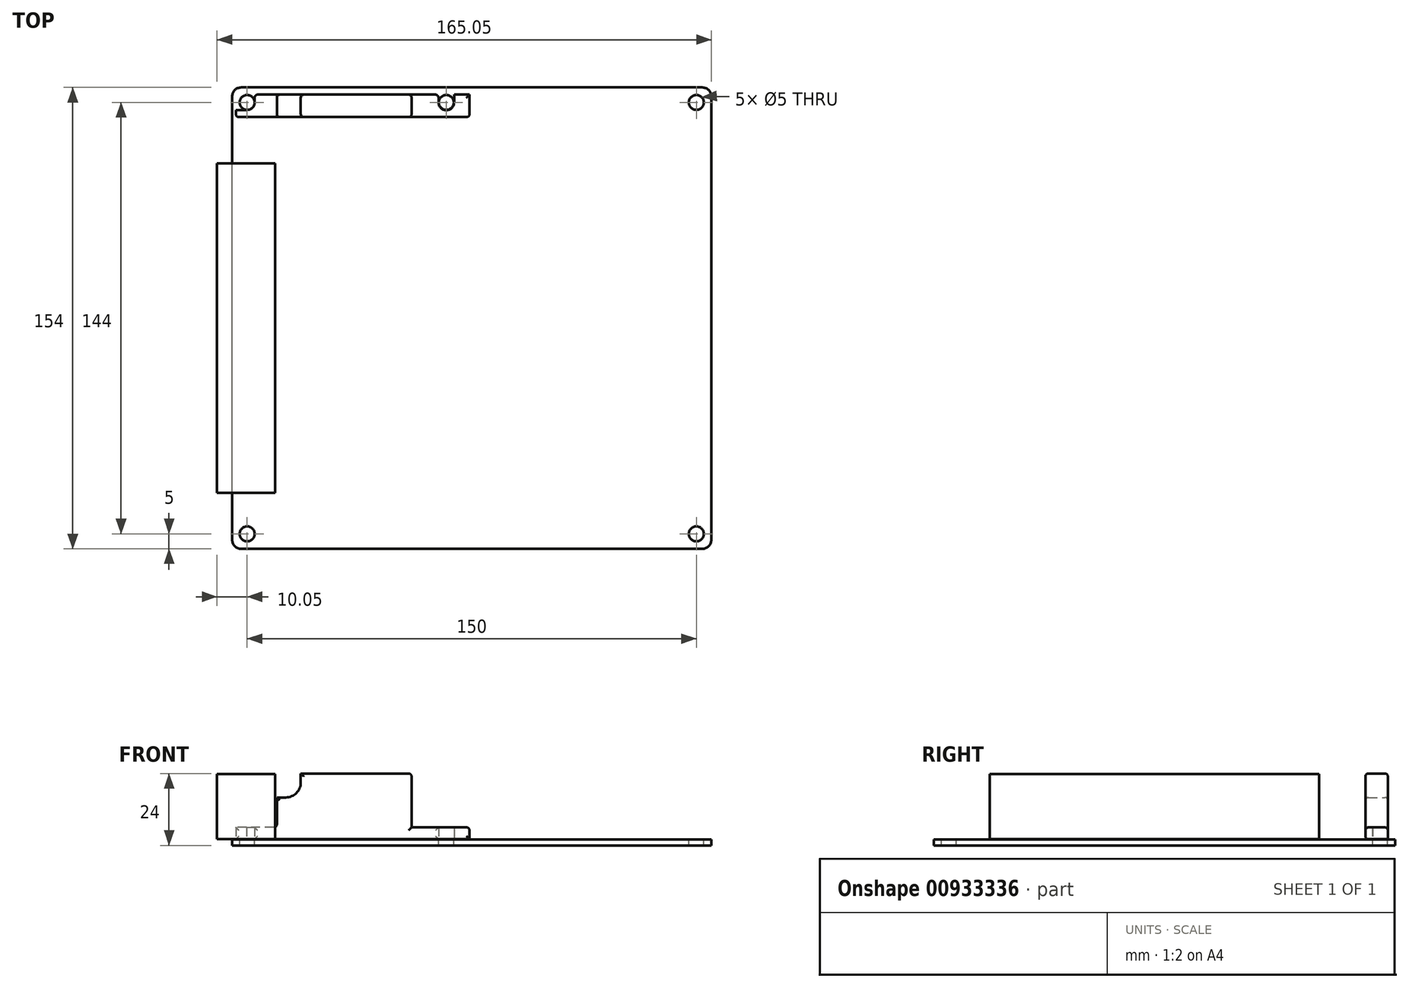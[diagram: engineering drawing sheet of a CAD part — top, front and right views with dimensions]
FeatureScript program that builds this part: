
annotation { "Feature Type Name" : "Feature", "Feature Type Description" : "" }
export const myFeature = defineFeature(function(context is Context, id is Id, definition is map)
    precondition{}
    {
        {
            var Q0;
            Q0=qCreatedBy(makeId("Top.planeOp"),FACE);
            var sketch = newSketch(context, id + "F0", { "sketchPlane" : qUnion([Q0])});
            skLineSegment(sketch, "E0.bottom", {"start": v(77, -77) * mm, "end": v(-77, -77) * mm});
            skLineSegment(sketch, "E0.top", {"start": v(77, 77) * mm, "end": v(-77, 77) * mm});
            skLineSegment(sketch, "E0.left", {"start": v(80, -74) * mm, "end": v(80, 74) * mm});
            skLineSegment(sketch, "E0.right", {"start": v(-80, -74) * mm, "end": v(-80, 74) * mm});
            skPoint(sketch, "E0.middle", {"position": v(0, 0) * mm});
            skPoint(sketch, "E1.visualSharp", {"position": v(80, 77) * mm});
            skArc(sketch, "E1.filletArc", {"start": v(80, 74) * mm, "mid": v(79.12, 76.12) * mm, "end": v(77, 77) * mm});
            skPoint(sketch, "E2.visualSharp", {"position": v(80, -77) * mm});
            skArc(sketch, "E2.filletArc", {"start": v(77, -77) * mm, "mid": v(79.12, -76.12) * mm, "end": v(80, -74) * mm});
            skPoint(sketch, "E3.visualSharp", {"position": v(-80, -77) * mm});
            skArc(sketch, "E3.filletArc", {"start": v(-80, -74) * mm, "mid": v(-79.12, -76.12) * mm, "end": v(-77, -77) * mm});
            skPoint(sketch, "E4.visualSharp", {"position": v(-80, 77) * mm});
            skArc(sketch, "E4.filletArc", {"start": v(-77, 77) * mm, "mid": v(-79.12, 76.12) * mm, "end": v(-80, 74) * mm});
            skSolve(sketch);
        }
        {
            var Q0;
            Q0 = qSketchRegion(id + "F0", true);
            extrude(context, id + "F1", {"entities" : qUnion([Q0]), "depth" : 2 * mm, "offsetDistance" : 25 * mm});
        }
        {
            var Q0;
            Q0=makeQuery(id+"F1.opExtrude","CAP_FACE",FACE,{"disambiguationData":[OSD([sQuery(id+"F0.wireOp",EDGE,"E0.bottom"),sQuery(id+"F0.wireOp",EDGE,"E0.top"),sQuery(id+"F0.wireOp",EDGE,"E0.left"),sQuery(id+"F0.wireOp",EDGE,"E0.right"),sQuery(id+"F0.wireOp",EDGE,"E1.filletArc"),sQuery(id+"F0.wireOp",EDGE,"E2.filletArc"),sQuery(id+"F0.wireOp",EDGE,"E3.filletArc"),sQuery(id+"F0.wireOp",EDGE,"E4.filletArc")])],"isStart":false});
            var sketch = newSketch(context, id + "F2", { "sketchPlane" : qUnion([Q0])});
            skCircle(sketch, "E5", {"center": v(75, 72) * mm, "radius": 2.5 * mm});
            skCircle(sketch, "E6", {"center": v(75, -72) * mm, "radius": 2.5 * mm});
            skCircle(sketch, "E7", {"center": v(-75, -72) * mm, "radius": 2.5 * mm});
            skCircle(sketch, "E8", {"center": v(-75, 72) * mm, "radius": 2.5 * mm});
            skLineSegment(sketch, "E9", {"start": v(77.5, -74.5) * mm, "end": v(-77.5, -74.5) * mm, "construction": true});
            skLineSegment(sketch, "E10", {"start": v(77.5, -74.5) * mm, "end": v(77.5, 74.5) * mm, "construction": true});
            skLineSegment(sketch, "E11", {"start": v(77.5, 74.5) * mm, "end": v(-77.5, 74.5) * mm, "construction": true});
            skLineSegment(sketch, "E12", {"start": v(-77.5, 74.5) * mm, "end": v(-77.5, -74.5) * mm, "construction": true});
            skCircle(sketch, "E13", {"center": v(-8.5, 72) * mm, "radius": 2.5 * mm});
            skSolve(sketch);
        }
        {
            var Q0;
            Q0 = qSketchRegion(id + "F2", true);
            extrude(context, id + "F3", {"entities" : qUnion([Q0]), "operationType" : NewBodyOperationType.REMOVE, "endBound" : BoundingType.UP_TO_NEXT, "oppositeDirection" : true, "depth" : 25 * mm, "offsetDistance" : 25 * mm});
        }
        {
            var Q0;
            Q0=makeQuery(id+"F1.opExtrude","CAP_FACE",FACE,{"disambiguationData":[OSD([sQuery(id+"F0.wireOp",EDGE,"E0.bottom"),sQuery(id+"F0.wireOp",EDGE,"E0.top"),sQuery(id+"F0.wireOp",EDGE,"E0.left"),sQuery(id+"F0.wireOp",EDGE,"E0.right"),sQuery(id+"F0.wireOp",EDGE,"E1.filletArc"),sQuery(id+"F0.wireOp",EDGE,"E2.filletArc"),sQuery(id+"F0.wireOp",EDGE,"E3.filletArc"),sQuery(id+"F0.wireOp",EDGE,"E4.filletArc")])],"isStart":false});
            var sketch = newSketch(context, id + "F4", { "sketchPlane" : qUnion([Q0])});
            skLineSegment(sketch, "E14.bottom", {"start": v(-65.61, 51.69) * mm, "end": v(-85.05, 51.69) * mm});
            skLineSegment(sketch, "E14.top", {"start": v(-65.61, -58.31) * mm, "end": v(-85.05, -58.31) * mm});
            skLineSegment(sketch, "E14.left", {"start": v(-65.61, 51.69) * mm, "end": v(-65.61, -58.31) * mm});
            skLineSegment(sketch, "E14.right", {"start": v(-85.05, 51.69) * mm, "end": v(-85.05, -58.31) * mm});
            skSolve(sketch);
        }
        {
            var Q0;
            Q0 = qSketchRegion(id + "F4", true);
            extrude(context, id + "F5", {"entities" : qUnion([Q0]), "operationType" : NewBodyOperationType.ADD, "depth" : 21.85 * mm, "offsetDistance" : 25 * mm, "hasSecondDirection" : true, "secondDirectionOppositeDirection" : true, "secondDirectionDepth" : -.1 * mm});
        }
        {
            var Q0;
            Q0=makeQuery(id+"F1.opExtrude","CAP_FACE",FACE,{"disambiguationData":[OSD([sQuery(id+"F0.wireOp",EDGE,"E0.bottom"),sQuery(id+"F0.wireOp",EDGE,"E0.top"),sQuery(id+"F0.wireOp",EDGE,"E0.left"),sQuery(id+"F0.wireOp",EDGE,"E0.right"),sQuery(id+"F0.wireOp",EDGE,"E1.filletArc"),sQuery(id+"F0.wireOp",EDGE,"E2.filletArc"),sQuery(id+"F0.wireOp",EDGE,"E3.filletArc"),sQuery(id+"F0.wireOp",EDGE,"E4.filletArc")])],"isStart":false});
            var sketch = newSketch(context, id + "F6", { "sketchPlane" : qUnion([Q0])});
            skLineSegment(sketch, "E15.bottom", {"start": v(-0.75, 67.1) * mm, "end": v(-78.75, 67.1) * mm});
            skLineSegment(sketch, "E15.top", {"start": v(-0.75, 74.6) * mm, "end": v(-5.9, 74.6) * mm});
            skLineSegment(sketch, "E15.left", {"start": v(-0.75, 67.1) * mm, "end": v(-0.75, 74.6) * mm});
            skLineSegment(sketch, "E15.right", {"start": v(-78.75, 67.1) * mm, "end": v(-78.75, 69.5) * mm});
            skLineSegment(sketch, "E16", {"start": v(-75.15, 69.5) * mm, "end": v(-78.75, 69.5) * mm});
            skLineSegment(sketch, "E17", {"start": v(-72.5, 71.95) * mm, "end": v(-72.5, 74.6) * mm});
            skArc(sketch, "E18", {"start": v(-75.15, 69.5) * mm, "mid": v(-73.3, 70.15) * mm, "end": v(-72.5, 71.95) * mm});
            skArc(sketch, "E19.0", {"start": v(-11.1, 72) * mm, "mid": v(-8.5, 69.4) * mm, "end": v(-5.9, 72) * mm});
            skLineSegment(sketch, "E20", {"start": v(-11.1, 72) * mm, "end": v(-11.1, 74.6) * mm});
            skLineSegment(sketch, "E21", {"start": v(-5.9, 72) * mm, "end": v(-5.9, 74.6) * mm});
            skLineSegment(sketch, "E22.trimOffspring", {"start": v(-11.1, 74.6) * mm, "end": v(-72.5, 74.6) * mm});
            skSolve(sketch);
        }
        {
            var Q0;
            Q0 = qSketchRegion(id + "F6", true);
            extrude(context, id + "F7", {"entities" : qUnion([Q0]), "operationType" : NewBodyOperationType.ADD, "depth" : 4 * mm, "offsetDistance" : 25 * mm, "hasSecondDirection" : true, "secondDirectionOppositeDirection" : true, "secondDirectionDepth" : -.1 * mm});
        }
        {
            var Q0;
            Q0=makeQuery(id+"F7.opExtrude","CAP_FACE",FACE,{"disambiguationData":[OSD([sQuery(id+"F6.wireOp",EDGE,"E15.bottom"),sQuery(id+"F6.wireOp",EDGE,"E15.top"),sQuery(id+"F6.wireOp",EDGE,"E15.left"),sQuery(id+"F6.wireOp",EDGE,"E15.right"),sQuery(id+"F6.wireOp",EDGE,"E16"),sQuery(id+"F6.wireOp",EDGE,"E17"),sQuery(id+"F6.wireOp",EDGE,"E18"),sQuery(id+"F6.wireOp",EDGE,"E19.0"),sQuery(id+"F6.wireOp",EDGE,"E20"),sQuery(id+"F6.wireOp",EDGE,"E21"),sQuery(id+"F6.wireOp",EDGE,"E22.trimOffspring")])],"isStart":false});
            var sketch = newSketch(context, id + "F8", { "sketchPlane" : qUnion([Q0])});
            skLineSegment(sketch, "E23.bottom", {"start": v(-20.1, 67.1) * mm, "end": v(-65.08, 67.1) * mm});
            skLineSegment(sketch, "E23.top", {"start": v(-20.1, 74.6) * mm, "end": v(-65.08, 74.6) * mm});
            skLineSegment(sketch, "E23.left", {"start": v(-20.1, 67.1) * mm, "end": v(-20.1, 74.6) * mm});
            skLineSegment(sketch, "E23.right", {"start": v(-65.08, 67.1) * mm, "end": v(-65.08, 74.6) * mm});
            skSolve(sketch);
        }
        {
            var Q0;
            Q0=makeQuery(id+"F8.imprint","IMPRINT",FACE,{"disambiguationData":[TD([[makeQuery(id+"F8.imprint","IMPRINT",EDGE,{"derivedFrom":sQuery(id+"F8.wireOp",EDGE,"E23.bottom")}),-1.0]])]});
            extrude(context, id + "F9", {"entities" : qUnion([Q0]), "operationType" : NewBodyOperationType.ADD, "depth" : 18 * mm, "offsetDistance" : 25 * mm});
        }
        {
            var Q0;
            Q0=makeQuery(id+"F9.boolean.opBoolean","MERGE",FACE,{"derivedFrom":[makeQuery(id+"F7.opExtrude","SWEPT_FACE",FACE,{"disambiguationData":[OSD([sQuery(id+"F6.wireOp",EDGE,"E22.trimOffspring")])]}),makeQuery(id+"F9.opExtrude","SWEPT_FACE",FACE,{"disambiguationData":[OSD([sQuery(id+"F8.wireOp",EDGE,"E23.top")])]})]});
            var sketch = newSketch(context, id + "F10", { "sketchPlane" : qUnion([Q0])});
            skLineSegment(sketch, "E24.bottom", {"start": v(57.1, 24) * mm, "end": v(65.08, 24) * mm});
            skLineSegment(sketch, "E24.top", {"start": v(57.1, 16.01) * mm, "end": v(65.08, 16.01) * mm});
            skLineSegment(sketch, "E24.left", {"start": v(57.1, 24) * mm, "end": v(57.1, 16.01) * mm});
            skLineSegment(sketch, "E24.right", {"start": v(65.08, 24) * mm, "end": v(65.08, 16.01) * mm});
            skSolve(sketch);
        }
        {
            var Q0;
            Q0 = qSketchRegion(id + "F10", true);
            extrude(context, id + "F11", {"entities" : qUnion([Q0]), "operationType" : NewBodyOperationType.REMOVE, "endBound" : BoundingType.UP_TO_NEXT, "oppositeDirection" : true, "depth" : 25 * mm, "offsetDistance" : 25 * mm});
        }
        {
            var Q0;
            Q0=makeQuery(id+"F11.boolean.opBoolean","COPY",EDGE,{"derivedFrom":makeQuery(id+"F11.opExtrude","SWEPT_EDGE",EDGE,{"disambiguationData":[OSD([sQuery(id+"F10.wireOp",EDGE,"E24.top"),sQuery(id+"F10.wireOp",EDGE,"E24.left")])]})});
            fillet(context, id + "F12", {"entities" : qUnion([Q0]), "radius" : 5 * mm, "tangentPropagation" : true, "allowEdgeOverflow" : false});
        }
        {
            var Q0;
            {var subQ0=sQuery(id+"F6.wireOp",EDGE,"E22.trimOffspring");var subQ1=sQuery(id+"F6.wireOp",EDGE,"E20");Q0=makeQuery(id+"F9.boolean.opBoolean","SPLIT",EDGE,{"disambiguationData":[TD([makeQuery(id+"F7.opExtrude","SWEPT_FACE",FACE,{"disambiguationData":[OSD([subQ1])]})])],"derivedFrom":makeQuery(id+"F7.opExtrude","CAP_EDGE",EDGE,{"disambiguationData":[OSD([subQ0])],"isStart":false})});}
            var Q1;
            Q1=makeQuery(id+"F9.opExtrude","SWEPT_EDGE",EDGE,{"disambiguationData":[OSD([sQuery(id+"F6.wireOp",EDGE,"E22.trimOffspring"),sQuery(id+"F8.wireOp",EDGE,"E23.top"),sQuery(id+"F8.wireOp",EDGE,"E23.left")])]});
            var Q2;
            Q2=makeQuery(id+"F9.opExtrude","CAP_EDGE",EDGE,{"disambiguationData":[OSD([sQuery(id+"F8.wireOp",EDGE,"E23.top")])],"isStart":false});
            var Q3;
            Q3=makeQuery(id+"F9.opExtrude","CAP_EDGE",EDGE,{"disambiguationData":[OSD([sQuery(id+"F8.wireOp",EDGE,"E23.right")])],"isStart":true});
            var Q4;
            Q4=makeQuery(id+"F9.opExtrude","SWEPT_EDGE",EDGE,{"disambiguationData":[OSD([sQuery(id+"F6.wireOp",EDGE,"E22.trimOffspring"),sQuery(id+"F8.wireOp",EDGE,"E23.top"),sQuery(id+"F8.wireOp",EDGE,"E23.right")])]});
            var Q5;
            Q5=makeQuery(id+"F9.boolean.opBoolean","MERGE",FACE,{"derivedFrom":[makeQuery(id+"F7.opExtrude","SWEPT_FACE",FACE,{"disambiguationData":[OSD([sQuery(id+"F6.wireOp",EDGE,"E22.trimOffspring")])]}),makeQuery(id+"F9.opExtrude","SWEPT_FACE",FACE,{"disambiguationData":[OSD([sQuery(id+"F8.wireOp",EDGE,"E23.top")])]})]});
            var Q6;
            Q6=makeQuery(id+"F9.boolean.opBoolean","MERGE",FACE,{"derivedFrom":[makeQuery(id+"F7.opExtrude","SWEPT_FACE",FACE,{"disambiguationData":[OSD([sQuery(id+"F6.wireOp",EDGE,"E15.bottom")])]}),makeQuery(id+"F9.opExtrude","SWEPT_FACE",FACE,{"disambiguationData":[OSD([sQuery(id+"F8.wireOp",EDGE,"E23.bottom")])]})]});
            var Q7;
            Q7=makeQuery(id+"F9.opExtrude","CAP_EDGE",EDGE,{"disambiguationData":[OSD([sQuery(id+"F8.wireOp",EDGE,"E23.left")])],"isStart":false});
            var Q8;
            Q8=makeQuery(id+"F9.opExtrude","CAP_EDGE",EDGE,{"disambiguationData":[OSD([sQuery(id+"F8.wireOp",EDGE,"E23.left")])],"isStart":true});
            var Q9;
            Q9=makeQuery(id+"F7.opExtrude","CAP_EDGE",EDGE,{"disambiguationData":[OSD([sQuery(id+"F6.wireOp",EDGE,"E15.left")])],"isStart":false});
            var Q10;
            Q10=makeQuery(id+"F7.opExtrude","CAP_EDGE",EDGE,{"disambiguationData":[OSD([sQuery(id+"F6.wireOp",EDGE,"E15.top")])],"isStart":false});
            fillet(context, id + "F13", {"entities" : qUnion([Q0, Q1, Q2, Q3, Q4, Q5, Q6, Q7, Q8, Q9, Q10]), "radius" : 1 * mm, "tangentPropagation" : true, "allowEdgeOverflow" : false});
        }
    });
